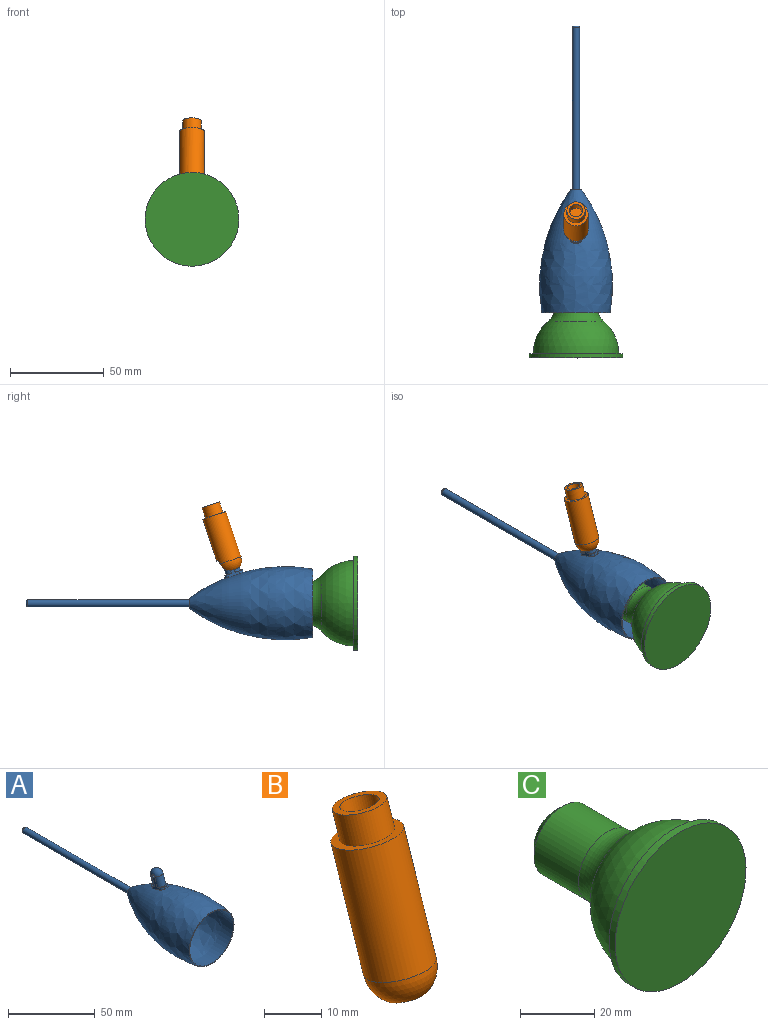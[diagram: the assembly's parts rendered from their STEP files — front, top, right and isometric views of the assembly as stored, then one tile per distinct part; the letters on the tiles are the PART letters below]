
ASSEMBLY  parts=3 mates=2
PART A: 28 faces, bbox 39.2x153.2x45.3 mm
  f0: plane 4.95x4.95mm, normal (0,1,0), area 7.8mm2, adj f5,f27
  f1: revolved ~65.88x39mm, area 13001mm2, adj f2,f13,f14,f15,f16,f23,f24,f25
  f2: plane 36.5x36.5mm, normal (0,-1,0), area 58.3mm2, adj f1,f4
  f3: plane 4.74x4.74mm, normal (0,-1,0), area 17.6mm2, adj f4
  f4: revolved ~65.49x37.98mm, area 12518.6mm2, adj f2,f3,f9,f10,f11,f12
  f5: cylinder r=1.91mm len=86mm, axis (0,-1,0), area 1029.4mm2, adj f0,f7
  f6: plane 1.81x1.81mm, normal (0,1,0), area 2.6mm2, adj f7
  f7: torus R=0.91mm, axis (0,1,0), area 15.2mm2, adj f5,f6
  f8: plane 9.49x5.9mm, normal (0,-0.32,-0.95), area 59mm2, adj f9,f10,f11,f12
  f9: plane 9.64x3.38mm, normal (-1,0,0), area 1.6mm2, adj f4,f8,f11,f12
  f10: plane 9.64x3.38mm, normal (1,0,0), area 1.6mm2, adj f4,f8,f11,f12
  f11: plane 6.12x0.55mm, normal (0,0.95,-0.32), area 1.4mm2, adj f4,f8,f9,f10
  f12: plane 6.07x0.5mm, normal (0,-0.95,0.32), area 1.5mm2, adj f4,f8,f9,f10
  f13: plane 1.92x1.37mm, normal (0,-0.95,0.32), area 2.7mm2, adj f1,f17,f24,f25
  f14: plane 1.93x1.38mm, normal (0,0.95,-0.32), area 2.7mm2, adj f1,f18,f23,f26
  f15: plane 9.97x6.58mm, normal (1,0,0), area 22mm2, adj f1,f17,f18,f19,f20,f21,f22,f23
  f16: plane 9.97x6.58mm, normal (-1,0,0), area 22mm2, adj f1,f17,f18,f19,f20,f21,f22,f25
  f17: plane 5.9x3.75mm, normal (0,0.32,0.95), area 7.9mm2, adj f13,f15,f16,f21,f24,f25
  f18: plane 5.9x3.75mm, normal (0,0.32,0.95), area 7.9mm2, adj f14,f15,f16,f20,f23,f26
  f19: cylinder r=1mm len=5.9mm, axis (-1,0,0), area 37.1mm2, adj f15,f16
  f20: cylinder r=2.95mm len=7.34mm, axis (0,-0.32,-0.95), area 62.6mm2, adj f15,f16,f18,f22
  f21: cylinder r=2.95mm len=7.34mm, axis (0,0.32,0.95), area 62.6mm2, adj f15,f16,f17,f22
  f22: torus R=1.05mm, axis (1,0,0), area 85.3mm2, adj f15,f16,f20,f21
  f23: cylinder r=2mm len=2.4mm, axis (0,-0.32,-0.95), area 4.7mm2, adj f1,f14,f15,f18
  f24: cylinder r=2mm len=2.39mm, axis (0,0.32,0.95), area 4.7mm2, adj f1,f13,f15,f17
  f25: cylinder r=2mm len=2.39mm, axis (0,-0.32,-0.95), area 4.7mm2, adj f1,f13,f16,f17
  f26: cylinder r=2mm len=2.4mm, axis (0,0.32,0.95), area 4.7mm2, adj f1,f14,f16,f18
  f27: torus R=2.47mm, axis (0,1,0), area 4.6mm2, adj f0,f1
PART B: 17 faces, bbox 13x21.1x37.3 mm
  f0: sphere r=5.5mm, area 88mm2, adj f1,f3,f4,f5,f12
  f1: cylinder r=5.5mm len=25.3mm, axis (0,-0.32,-0.95), area 776mm2, adj f0,f2,f6,f10,f11,f12
  f2: plane 11x10.44mm, normal (0,-0.32,-0.95), area 95mm2, adj f1
  f3: cylinder r=4mm len=8mm, axis (0,-0.32,-0.95), area 16.9mm2, adj f0,f4,f5,f7
  f4: plane 6.48x3.93mm, normal (1,0,0), area 9.4mm2, adj f0,f3,f7,f11
  f5: plane 6.48x3.93mm, normal (-1,0,0), area 9.4mm2, adj f0,f3,f7,f10
  f6: plane 4x1.31mm, normal (0,-0.32,-0.95), area 4.1mm2, adj f1,f9,f10,f11
  f7: sphere r=6.5mm, area 155.7mm2, adj f3,f4,f5,f9
  f8: plane 13x12.33mm, normal (0,0.32,0.95), area 57.3mm2, adj f9,f14
  f9: cylinder r=6.5mm len=28.3mm, axis (0,-0.32,-0.95), area 1026.3mm2, adj f6,f7,f8,f10,f11
  f10: cylinder r=2mm len=2.92mm, axis (0,0.95,-0.32), area 3.8mm2, adj f1,f5,f6,f9
  f11: cylinder r=2mm len=2.92mm, axis (0,-0.95,0.32), area 3.8mm2, adj f1,f4,f6,f9
  f12: cylinder r=1mm len=11mm, axis (-1,0,0), area 68.3mm2, adj f0,f1
  f13: cylinder r=3.5mm len=8.54mm, axis (0,-0.32,-0.95), area 131.9mm2, adj f15,f16
  f14: cylinder r=4.9mm len=11.19mm, axis (0,-0.32,-0.95), area 184.7mm2, adj f8,f15
  f15: plane 9.8x9.3mm, normal (0,0.32,0.95), area 36.9mm2, adj f13,f14
  f16: plane 7x6.64mm, normal (0,0.32,0.95), area 38.5mm2, adj f13
PART C: 8 faces, bbox 50x48x50 mm
  f0: plane 50x50mm, normal (0,-1,0), area 1963.5mm2, adj f6
  f1: plane 16x16mm, normal (0,1,0), area 201.1mm2, adj f7
  f2: cylinder r=11mm len=22mm, axis (0,-1,0), area 1175mm2, adj f3,f7
  f3: torus R=22.09mm, axis (0,-1,0), area 738.8mm2, adj f2,f4
  f4: sphere r=22.8mm, area 2477.1mm2, adj f3,f5
  f5: plane 50x50mm, normal (0,1,0), area 330.4mm2, adj f4,f6
  f6: cylinder r=25mm len=50mm, axis (0,-1,0), area 361.3mm2, adj f0,f5
  f7: cone r=11mm half-angle=45deg, axis (0,-1,0), area 253.2mm2, adj f1,f2
PLACE A at identity fixed
PLACE B at identity
PLACE C rot(axis=(0,1,0),90deg) t=(0,0,0)mm
MATE revolute B.f12 <-> A.f19  axis (-1,0,0) through (0,44.53,22.66)mm
MATE fastened C.f2 <-> A.f5  axis (0,1,0) through (0,24,0)mm
